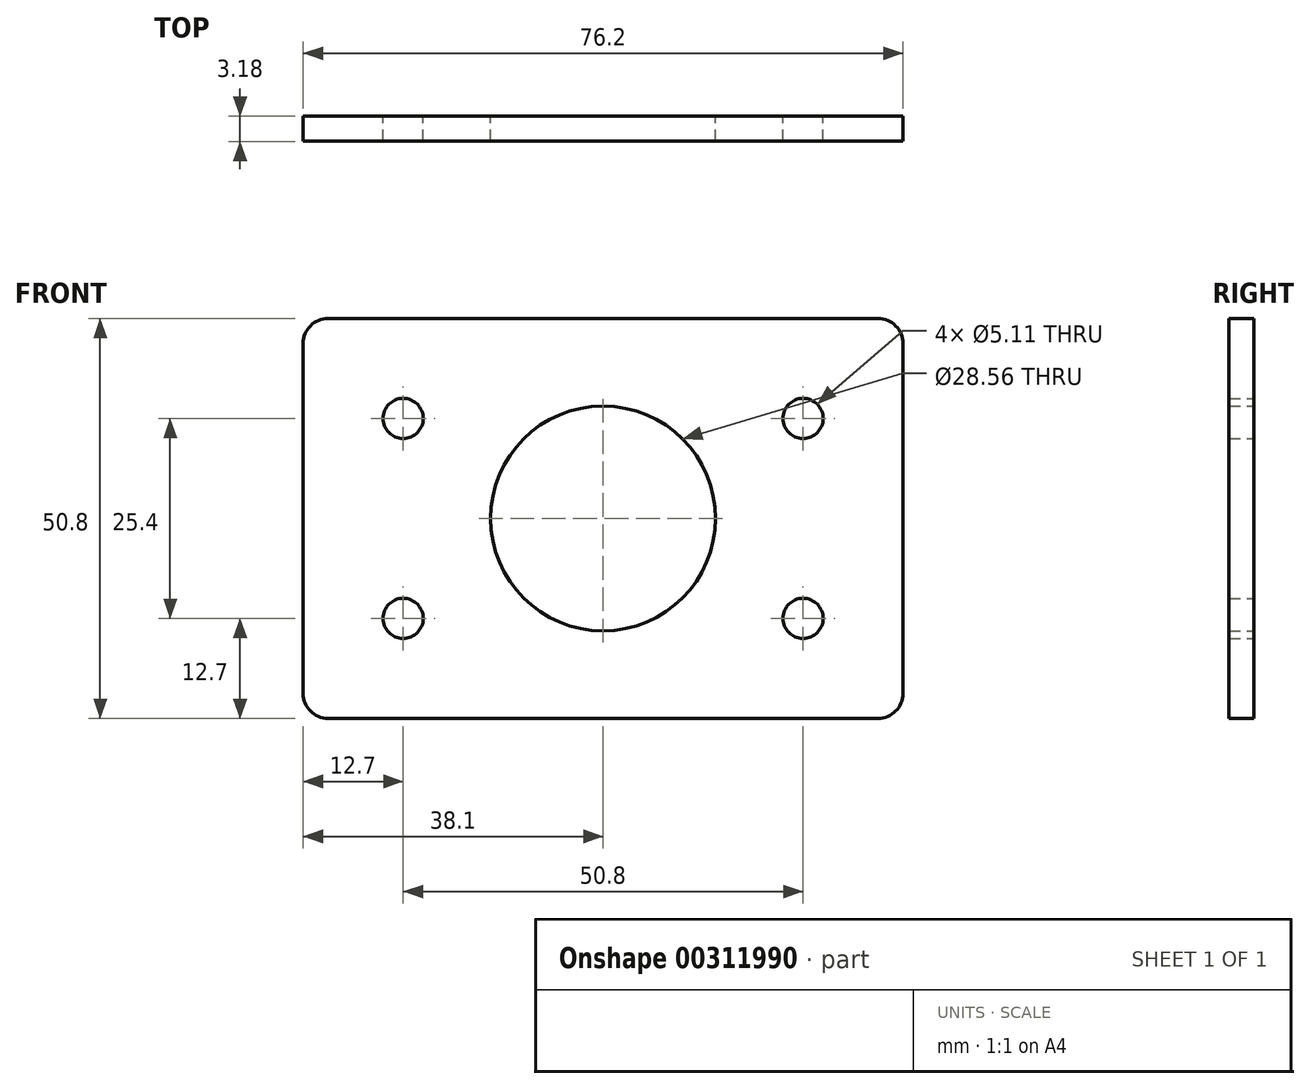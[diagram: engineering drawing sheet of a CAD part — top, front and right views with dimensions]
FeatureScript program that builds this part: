
annotation { "Feature Type Name" : "Feature", "Feature Type Description" : "" }
export const myFeature = defineFeature(function(context is Context, id is Id, definition is map)
    precondition{}
    {
        {
            var Q0;
            Q0=qCreatedBy(makeId("Front.planeOp"),FACE);
            var sketch = newSketch(context, id + "F0", { "sketchPlane" : qUnion([Q0])});
            skLineSegment(sketch, "E0.bottom", {"start": v(38.1, -25.4) * mm, "end": v(-38.1, -25.4) * mm});
            skLineSegment(sketch, "E0.top", {"start": v(38.1, 25.4) * mm, "end": v(-38.1, 25.4) * mm});
            skLineSegment(sketch, "E0.left", {"start": v(38.1, -25.4) * mm, "end": v(38.1, 25.4) * mm});
            skLineSegment(sketch, "E0.right", {"start": v(-38.1, -25.4) * mm, "end": v(-38.1, 25.4) * mm});
            skPoint(sketch, "E0.middle", {"position": v(0, 0) * mm});
            skCircle(sketch, "E1", {"center": v(0, 0) * mm, "radius": 14.28 * mm});
            skLineSegment(sketch, "E2.bottom", {"start": v(25.4, 12.7) * mm, "end": v(-25.4, 12.7) * mm, "construction": true});
            skLineSegment(sketch, "E2.top", {"start": v(25.4, -12.7) * mm, "end": v(-25.4, -12.7) * mm, "construction": true});
            skLineSegment(sketch, "E2.left", {"start": v(25.4, 12.7) * mm, "end": v(25.4, -12.7) * mm, "construction": true});
            skLineSegment(sketch, "E2.right", {"start": v(-25.4, 12.7) * mm, "end": v(-25.4, -12.7) * mm, "construction": true});
            skCircle(sketch, "E3", {"center": v(-25.4, 12.7) * mm, "radius": 2.55 * mm});
            skCircle(sketch, "E4", {"center": v(25.4, 12.7) * mm, "radius": 2.55 * mm});
            skCircle(sketch, "E5", {"center": v(25.4, -12.7) * mm, "radius": 2.55 * mm});
            skCircle(sketch, "E6", {"center": v(-25.4, -12.7) * mm, "radius": 2.55 * mm});
            skSolve(sketch);
        }
        {
            var Q0;
            Q0=makeQuery(id+"F0.imprint","IMPRINT",FACE,{"disambiguationData":[TD([[makeQuery(id+"F0.imprint","IMPRINT",EDGE,{"derivedFrom":sQuery(id+"F0.wireOp",EDGE,"E0.bottom")}),-1.0]])]});
            extrude(context, id + "F1", {"entities" : qUnion([Q0]), "depth" : 3.17 * mm});
        }
        {
            var Q0;
            Q0=makeQuery(id+"F1.opExtrude","SWEPT_EDGE",EDGE,{"disambiguationData":[OSD([sQuery(id+"F0.wireOp",EDGE,"E0.top"),sQuery(id+"F0.wireOp",EDGE,"E0.right")])]});
            var Q1;
            Q1=makeQuery(id+"F1.opExtrude","SWEPT_EDGE",EDGE,{"disambiguationData":[OSD([sQuery(id+"F0.wireOp",EDGE,"E0.bottom"),sQuery(id+"F0.wireOp",EDGE,"E0.right")])]});
            var Q2;
            Q2=makeQuery(id+"F1.opExtrude","SWEPT_EDGE",EDGE,{"disambiguationData":[OSD([sQuery(id+"F0.wireOp",EDGE,"E0.bottom"),sQuery(id+"F0.wireOp",EDGE,"E0.left")])]});
            var Q3;
            Q3=makeQuery(id+"F1.opExtrude","SWEPT_EDGE",EDGE,{"disambiguationData":[OSD([sQuery(id+"F0.wireOp",EDGE,"E0.top"),sQuery(id+"F0.wireOp",EDGE,"E0.left")])]});
            fillet(context, id + "F2", {"entities" : qUnion([Q0, Q1, Q2, Q3]), "radius" : 3.17 * mm, "tangentPropagation" : true, "allowEdgeOverflow" : false});
        }
    });
